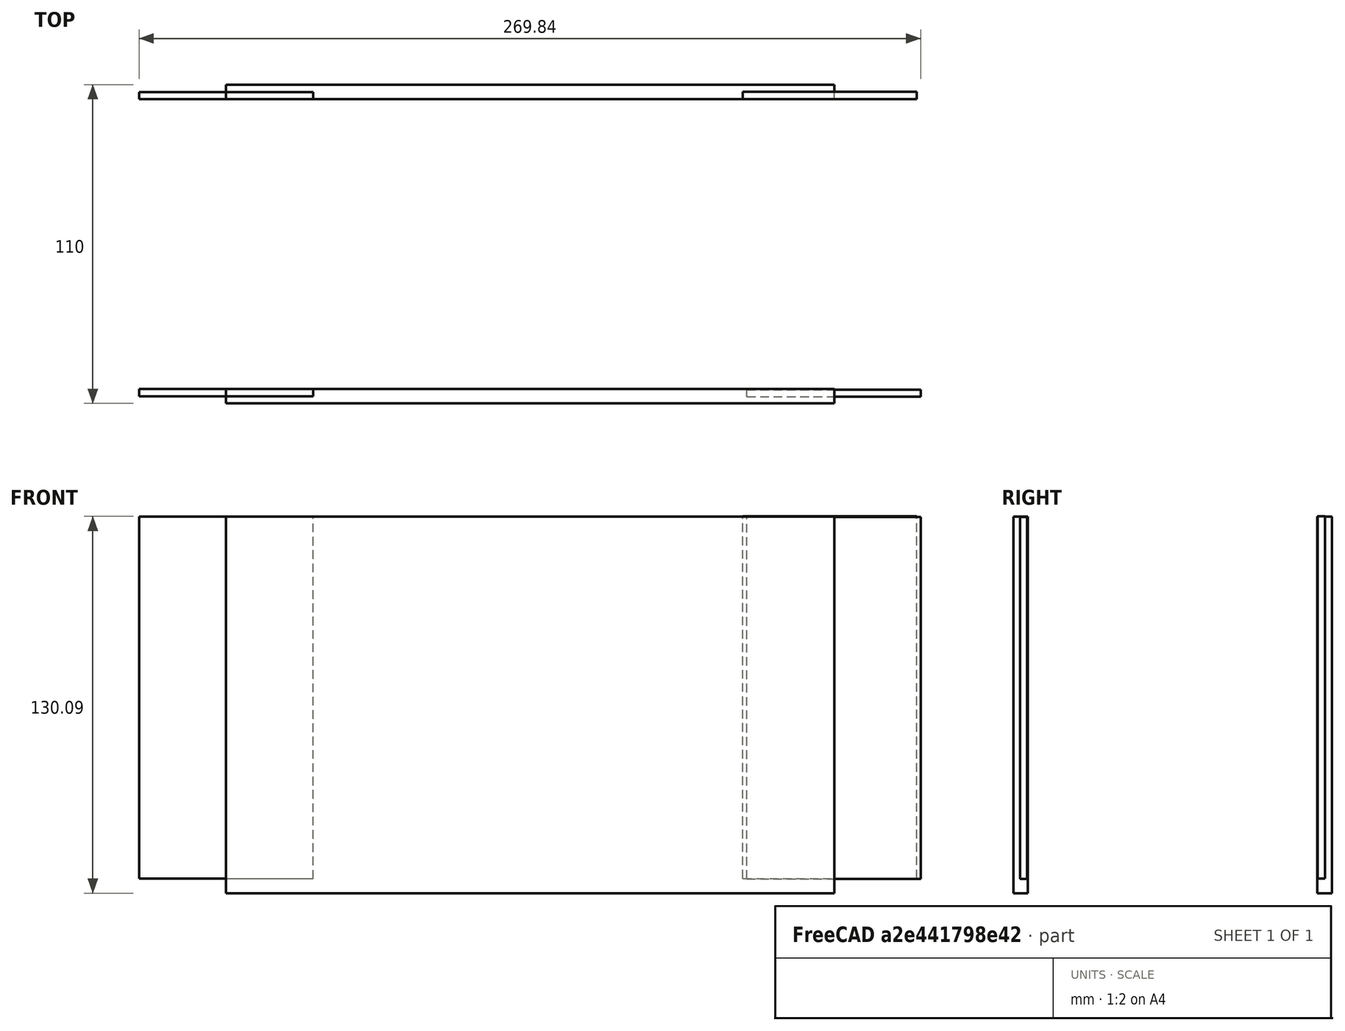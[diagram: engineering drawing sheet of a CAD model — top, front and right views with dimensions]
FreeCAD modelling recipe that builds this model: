
FCSTD DOCUMENT  (FreeCAD 0.19R24291 (Git))
Label: w maze middle
License: All rights reserved
LicenseURL: http://en.wikipedia.org/wiki/All_rights_reserved
objects: Part::Box×6, App::MeasureDistance×2
note: 6 computed .brp shape members not serialized (recipe doc carries the construction recipe); baked Part::Feature solids carry a one-line shape summary decoded from their .brp

FEATURE [Part::Box] Box009  label="Cube009"
  AttacherType = Attacher::AttachEngine3D
  Height = 125
  Length = 60
  Placement = pos=(-30,2.5,5) rot=(0,0,1;0rad)
  Width = 2.5
FEATURE [Part::Box] Box002  label="Cube002"
  AttacherType = Attacher::AttachEngine3D
  Height = 130
  Length = 210
  Placement = pos=(0,105,0) rot=(0,0,1;0rad)
  Width = 5
FEATURE [Part::Box] Box003  label="Cube003"
  AttacherType = Attacher::AttachEngine3D
  Height = 130
  Length = 210
  Width = 5
FEATURE [Part::Box] Box011  label="Cube011"
  AttacherType = Attacher::AttachEngine3D
  Height = 125
  Length = 60
  Placement = pos=(178.45,105.069,5.09117) rot=(0,0,1;0rad)
  Width = 2.5
FEATURE [Part::Box] Box012  label="Cube012"
  AttacherType = Attacher::AttachEngine3D
  Height = 125
  Length = 60
  Placement = pos=(-30,105,5) rot=(0,0,1;0rad)
  Width = 2.5
FEATURE [Part::Box] Box013  label="Cube013"
  AttacherType = Attacher::AttachEngine3D
  Height = 125
  Length = 60
  Placement = pos=(179.84,2.26451,4.90105) rot=(0,0,1;0rad)
  Width = 2.5
FEATURE [App::MeasureDistance] Distance001  label="Distance: 240.01 mm"
  Distance = 240.013
  P1 = (-30,2.5,130)
  P2 = (210,0,130)
FEATURE [App::MeasureDistance] Distance  label="Distance: 100.00 mm"
  Distance = 100.001
  P1 = (-29.9129,5,130)
  P2 = (-29.5937,105,130)
